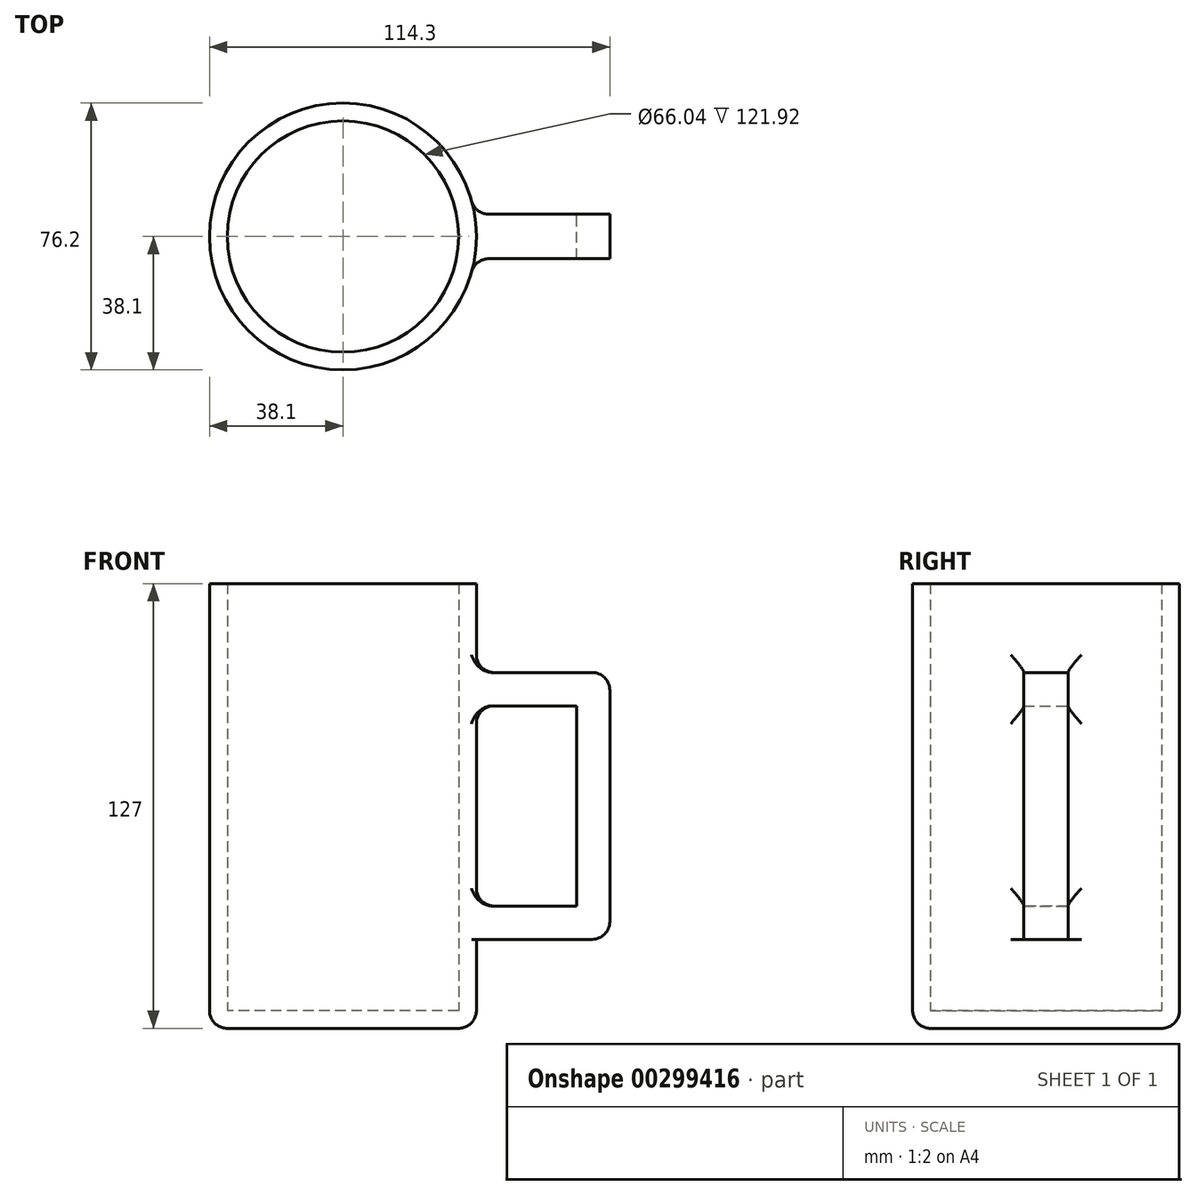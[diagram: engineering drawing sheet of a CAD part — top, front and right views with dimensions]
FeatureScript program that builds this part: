
annotation { "Feature Type Name" : "Feature", "Feature Type Description" : "" }
export const myFeature = defineFeature(function(context is Context, id is Id, definition is map)
    precondition{}
    {
        {
            var Q0;
            Q0=qCreatedBy(makeId("Top.planeOp"),FACE);
            var sketch = newSketch(context, id + "F0", { "sketchPlane" : qUnion([Q0])});
            skCircle(sketch, "E0", {"center": v(0, 0) * mm, "radius": 38.1 * mm});
            skSolve(sketch);
        }
        {
            var Q0;
            Q0=makeQuery(id+"F0.imprint","IMPRINT",FACE,{"disambiguationData":[TD([[makeQuery(id+"F0.imprint","IMPRINT",EDGE,{"derivedFrom":sQuery(id+"F0.wireOp",EDGE,"E0")}),1.0]])]});
            extrude(context, id + "F1", {"entities" : qUnion([Q0]), "depth" : 127 * mm});
        }
        {
            var Q0;
            Q0=makeQuery(id+"F1.opExtrude","CAP_FACE",FACE,{"disambiguationData":[OSD([sQuery(id+"F0.wireOp",EDGE,"E0")])],"isStart":false});
            shell(context, id + "F2", {"entities" : qUnion([Q0]), "thickness" : 5.08 * mm});
        }
        {
            var Q0;
            Q0=qCreatedBy(makeId("Front.planeOp"),FACE);
            var sketch = newSketch(context, id + "F3", { "sketchPlane" : qUnion([Q0])});
            skLineSegment(sketch, "E1", {"start": v(38.1, 101.6) * mm, "end": v(76.2, 101.6) * mm});
            skLineSegment(sketch, "E2", {"start": v(76.2, 25.4) * mm, "end": v(38.1, 25.4) * mm});
            skLineSegment(sketch, "E3", {"start": v(38.1, 25.4) * mm, "end": v(76.2, 25.4) * mm});
            skLineSegment(sketch, "E4", {"start": v(76.2, 101.6) * mm, "end": v(76.2, 25.4) * mm});
            skLineSegment(sketch, "E5", {"start": v(38.1, 92.08) * mm, "end": v(66.67, 92.08) * mm});
            skLineSegment(sketch, "E6", {"start": v(66.67, 92.08) * mm, "end": v(66.67, 34.92) * mm});
            skLineSegment(sketch, "E7", {"start": v(66.68, 34.92) * mm, "end": v(38.1, 34.92) * mm});
            skLineSegment(sketch, "E8", {"start": v(38.1, 34.92) * mm, "end": v(38.1, 25.4) * mm});
            skLineSegment(sketch, "E9", {"start": v(38.1, 92.08) * mm, "end": v(38.1, 101.6) * mm});
            skLineSegment(sketch, "E10", {"start": v(-38.1, 0) * mm, "end": v(-38.1, 127) * mm});
            skLineSegment(sketch, "E11", {"start": v(66.67, 63.5) * mm, "end": v(76.2, 63.5) * mm, "construction": true});
            skLineSegment(sketch, "E12", {"start": v(38.1, 127) * mm, "end": v(38.1, 0) * mm, "construction": true});
            skSolve(sketch);
        }
        {
            var Q0;
            Q0=makeQuery(id+"F3.imprint","IMPRINT",FACE,{"disambiguationData":[TD([[makeQuery(id+"F3.imprint","IMPRINT",EDGE,{"derivedFrom":sQuery(id+"F3.wireOp",EDGE,"E1")}),-1.0]])]});
            extrude(context, id + "F4", {"entities" : qUnion([Q0]), "endBound" : BoundingType.SYMMETRIC, "depth" : 12.7 * mm});
        }
        {
            var Q0;
            Q0=makeQuery(id+"F4.opExtrude","SWEPT_FACE",FACE,{"disambiguationData":[OSD([sQuery(id+"F3.wireOp",EDGE,"E9")])]});
            var Q1;
            Q1=makeQuery(id+"F4.opExtrude","SWEPT_FACE",FACE,{"disambiguationData":[OSD([sQuery(id+"F3.wireOp",EDGE,"E8")])]});
            var Q2;
            {var subQ0=sQuery(id+"F0.wireOp",EDGE,"E0");Q2=makeQuery(id+"F2.opShell","OFFSET_FACE",FACE,{"disambiguationData":[OSD([subQ0]),TDD([makeQuery(id+"F1.opExtrude","SWEPT_FACE",FACE,{"disambiguationData":[OSD([subQ0])]})])]});}
            var Q3;
            Q3=makeQuery(id+"F1.opExtrude","SWEPT_BODY",BODY,{"disambiguationData":[OSD([sQuery(id+"F0.wireOp",EDGE,"E0")])]});
            extrude(context, id + "F5", {"entities" : qUnion([Q0, Q1]), "operationType" : NewBodyOperationType.ADD, "endBound" : BoundingType.UP_TO_SURFACE, "endBoundEntityFace" : qUnion([Q2]), "endBoundEntityBody" : qUnion([Q3]), "depth" : 25.4 * mm});
        }
        {
            var Q0;
            Q0=makeQuery(id+"F5.boolean.opBoolean","INTERSECT",EDGE,{"derivedFrom":[makeQuery(id+"F1.opExtrude","SWEPT_FACE",FACE,{"disambiguationData":[OSD([sQuery(id+"F0.wireOp",EDGE,"E0")])]}),makeQuery(id+"F5.opExtrude","SWEPT_FACE",FACE,{"disambiguationData":[OSD([sQuery(id+"F3.wireOp",EDGE,"E1"),sQuery(id+"F3.wireOp",EDGE,"E9")])]})]});
            var Q1;
            {var subQ0=sQuery(id+"F3.wireOp",EDGE,"E9");Q1=makeQuery(id+"F5.boolean.opBoolean","INTERSECT",EDGE,{"disambiguationData":[OD(0.0)],"derivedFrom":[makeQuery(id+"F1.opExtrude","SWEPT_FACE",FACE,{"disambiguationData":[OSD([sQuery(id+"F0.wireOp",EDGE,"E0")])]}),makeQuery(id+"F5.opExtrude","SWEPT_FACE",FACE,{"disambiguationData":[OSD([subQ0]),TDD([makeQuery(id+"F4.opExtrude","CAP_EDGE",EDGE,{"disambiguationData":[OSD([subQ0])],"isStart":false})])]})]});}
            var Q2;
            Q2=makeQuery(id+"F5.boolean.opBoolean","INTERSECT",EDGE,{"derivedFrom":[makeQuery(id+"F1.opExtrude","SWEPT_FACE",FACE,{"disambiguationData":[OSD([sQuery(id+"F0.wireOp",EDGE,"E0")])]}),makeQuery(id+"F5.opExtrude","SWEPT_FACE",FACE,{"disambiguationData":[OSD([sQuery(id+"F3.wireOp",EDGE,"E5"),sQuery(id+"F3.wireOp",EDGE,"E9")])]})]});
            var Q3;
            {var subQ0=sQuery(id+"F3.wireOp",EDGE,"E9");Q3=makeQuery(id+"F5.boolean.opBoolean","INTERSECT",EDGE,{"disambiguationData":[OD(0.0)],"derivedFrom":[makeQuery(id+"F1.opExtrude","SWEPT_FACE",FACE,{"disambiguationData":[OSD([sQuery(id+"F0.wireOp",EDGE,"E0")])]}),makeQuery(id+"F5.opExtrude","SWEPT_FACE",FACE,{"disambiguationData":[OSD([subQ0]),TDD([makeQuery(id+"F4.opExtrude","CAP_EDGE",EDGE,{"disambiguationData":[OSD([subQ0])],"isStart":true})])]})]});}
            var Q4;
            {var subQ0=sQuery(id+"F3.wireOp",EDGE,"E9");Q4=makeQuery(id+"F5.boolean.opBoolean","INTERSECT",EDGE,{"disambiguationData":[OD(1.0)],"derivedFrom":[makeQuery(id+"F1.opExtrude","SWEPT_FACE",FACE,{"disambiguationData":[OSD([sQuery(id+"F0.wireOp",EDGE,"E0")])]}),makeQuery(id+"F5.opExtrude","SWEPT_FACE",FACE,{"disambiguationData":[OSD([subQ0]),TDD([makeQuery(id+"F4.opExtrude","CAP_EDGE",EDGE,{"disambiguationData":[OSD([subQ0])],"isStart":true})])]})]});}
            var Q5;
            Q5=makeQuery(id+"F5.boolean.opBoolean","INTERSECT",EDGE,{"derivedFrom":[makeQuery(id+"F1.opExtrude","SWEPT_FACE",FACE,{"disambiguationData":[OSD([sQuery(id+"F0.wireOp",EDGE,"E0")])]}),makeQuery(id+"F5.opExtrude","SWEPT_FACE",FACE,{"disambiguationData":[OSD([sQuery(id+"F3.wireOp",EDGE,"E7"),sQuery(id+"F3.wireOp",EDGE,"E8")])]})]});
            var Q6;
            Q6=makeQuery(id+"F5.boolean.opBoolean","INTERSECT",EDGE,{"derivedFrom":[makeQuery(id+"F1.opExtrude","SWEPT_FACE",FACE,{"disambiguationData":[OSD([sQuery(id+"F0.wireOp",EDGE,"E0")])]}),makeQuery(id+"F5.opExtrude","SWEPT_FACE",FACE,{"disambiguationData":[OSD([sQuery(id+"F3.wireOp",EDGE,"E3"),sQuery(id+"F3.wireOp",EDGE,"E8")])]})]});
            var Q7;
            {var subQ0=sQuery(id+"F3.wireOp",EDGE,"E9");Q7=makeQuery(id+"F5.boolean.opBoolean","INTERSECT",EDGE,{"disambiguationData":[OD(1.0)],"derivedFrom":[makeQuery(id+"F1.opExtrude","SWEPT_FACE",FACE,{"disambiguationData":[OSD([sQuery(id+"F0.wireOp",EDGE,"E0")])]}),makeQuery(id+"F5.opExtrude","SWEPT_FACE",FACE,{"disambiguationData":[OSD([subQ0]),TDD([makeQuery(id+"F4.opExtrude","CAP_EDGE",EDGE,{"disambiguationData":[OSD([subQ0])],"isStart":false})])]})]});}
            var Q8;
            Q8=makeQuery(id+"F4.opExtrude","SWEPT_EDGE",EDGE,{"disambiguationData":[OSD([sQuery(id+"F3.wireOp",EDGE,"E3"),sQuery(id+"F3.wireOp",EDGE,"E4")])]});
            var Q9;
            Q9=makeQuery(id+"F4.opExtrude","SWEPT_EDGE",EDGE,{"disambiguationData":[OSD([sQuery(id+"F3.wireOp",EDGE,"E1"),sQuery(id+"F3.wireOp",EDGE,"E4")])]});
            var Q10;
            Q10=makeQuery(id+"F1.opExtrude","CAP_EDGE",EDGE,{"disambiguationData":[OSD([sQuery(id+"F0.wireOp",EDGE,"E0")])],"isStart":true});
            fillet(context, id + "F6", {"entities" : qUnion([Q0, Q1, Q2, Q3, Q4, Q5, Q6, Q7, Q8, Q9, Q10]), "radius" : 5.08 * mm, "tangentPropagation" : true, "allowEdgeOverflow" : false});
        }
    });
